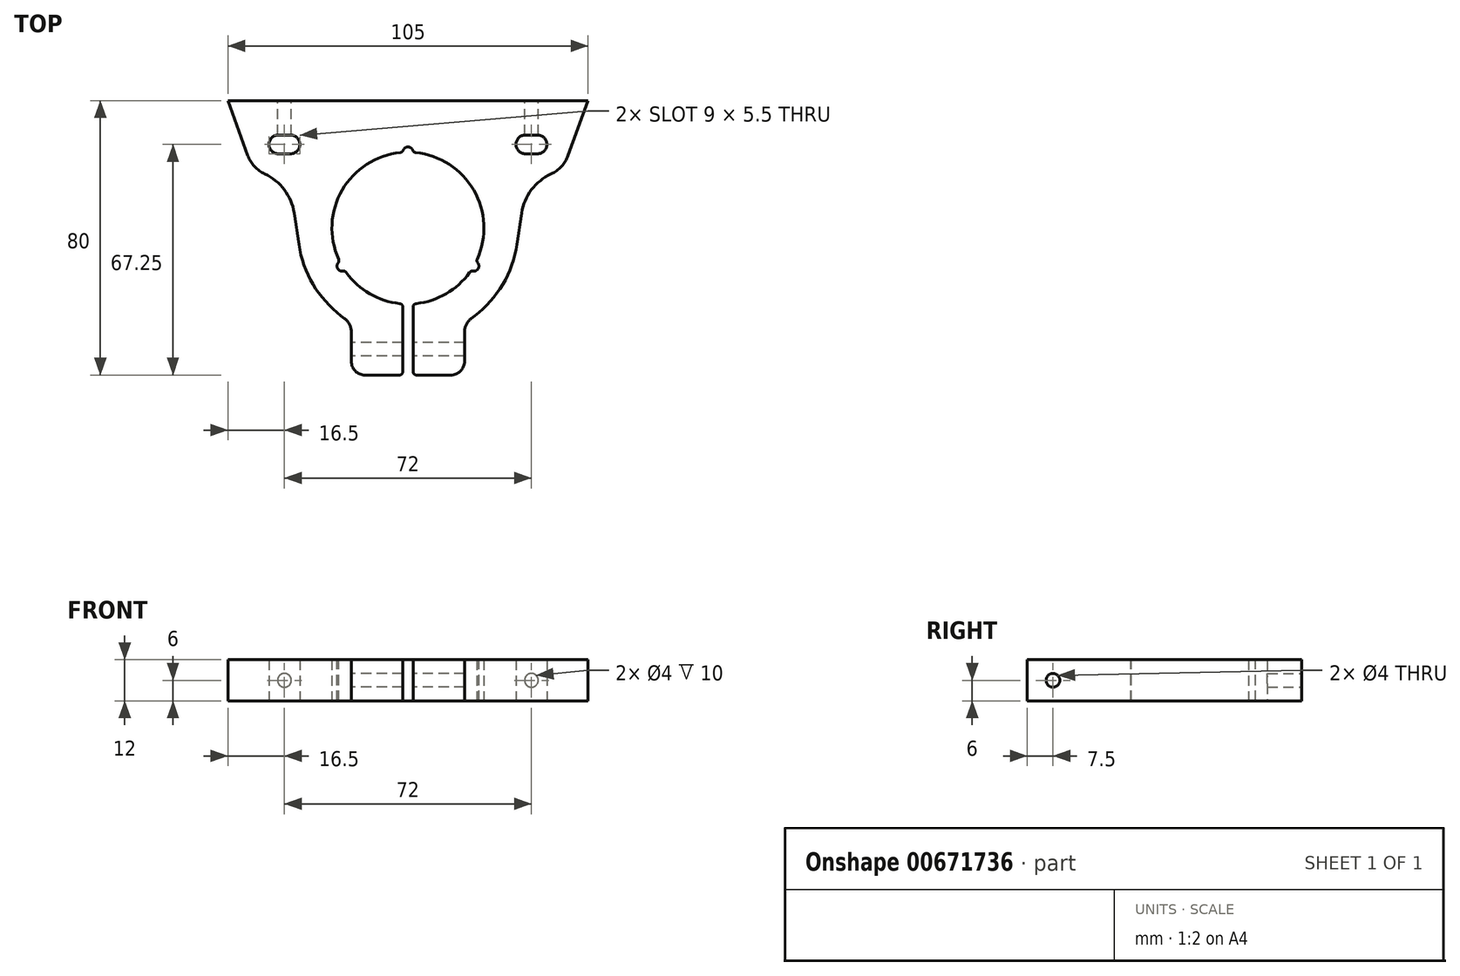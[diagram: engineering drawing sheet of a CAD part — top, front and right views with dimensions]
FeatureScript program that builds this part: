
annotation { "Feature Type Name" : "Feature", "Feature Type Description" : "" }
export const myFeature = defineFeature(function(context is Context, id is Id, definition is map)
    precondition{}
    {
        {
            var Q0;
            Q0=qCreatedBy(makeId("Top.planeOp"),FACE);
            var sketch = newSketch(context, id + "F0", { "sketchPlane" : qUnion([Q0])});
            skLineSegment(sketch, "E0", {"start": v(-52.5, 0) * mm, "end": v(52.5, 0) * mm});
            skLineSegment(sketch, "E1", {"start": v(-19.5, -62.71) * mm, "end": v(-16.5, -65) * mm});
            skLineSegment(sketch, "E2", {"start": v(-16.5, -65) * mm, "end": v(-16.5, -80) * mm});
            skLineSegment(sketch, "E3", {"start": v(-16.5, -80) * mm, "end": v(-1.5, -80) * mm});
            skLineSegment(sketch, "E4", {"start": v(-1.5, -80) * mm, "end": v(-1.5, -59.25) * mm});
            skArc(sketch, "E5", {"start": v(1.5, -59.25) * mm, "mid": v(0, -15) * mm, "end": v(-1.5, -59.25) * mm});
            skLineSegment(sketch, "E6.MirrorCS", {"start": v(16.5, -65) * mm, "end": v(16.5, -80) * mm});
            skLineSegment(sketch, "E7.MirrorCS", {"start": v(16.5, -80) * mm, "end": v(1.5, -80) * mm});
            skLineSegment(sketch, "E8.MirrorCS", {"start": v(1.5, -80) * mm, "end": v(1.5, -59.25) * mm});
            skCircle(sketch, "E9", {"center": v(0, -37.15) * mm, "radius": 32.15 * mm, "construction": true});
            skLineSegment(sketch, "E10", {"start": v(0, -37.15) * mm, "end": v(-19.5, -62.71) * mm, "construction": true});
            skLineSegment(sketch, "E11.bottom", {"start": v(-37.75, -15.5) * mm, "end": v(-34.25, -15.5) * mm});
            skLineSegment(sketch, "E11.top", {"start": v(-37.75, -10) * mm, "end": v(-34.25, -10) * mm});
            skArc(sketch, "E12", {"start": v(-37.75, -10) * mm, "mid": v(-40.5, -12.75) * mm, "end": v(-37.75, -15.5) * mm});
            skArc(sketch, "E13", {"start": v(-34.25, -15.5) * mm, "mid": v(-31.5, -12.75) * mm, "end": v(-34.25, -10) * mm});
            skLineSegment(sketch, "E14", {"start": v(0, 0) * mm, "end": v(0, -15) * mm, "construction": true});
            skLineSegment(sketch, "E15.MirrorCS", {"start": v(37.75, -15.5) * mm, "end": v(34.25, -15.5) * mm});
            skArc(sketch, "E16.MirrorCS", {"start": v(34.25, -15.5) * mm, "mid": v(31.5, -12.75) * mm, "end": v(34.25, -10) * mm});
            skArc(sketch, "E17.MirrorCS", {"start": v(37.75, -10) * mm, "mid": v(40.5, -12.75) * mm, "end": v(37.75, -15.5) * mm});
            skLineSegment(sketch, "E18.MirrorCS", {"start": v(37.75, -10) * mm, "end": v(34.25, -10) * mm});
            skArc(sketch, "E19.0", {"start": v(-46.68, -16) * mm, "mid": v(-44.74, -19.18) * mm, "end": v(-41.73, -21.38) * mm});
            skLineSegment(sketch, "E20", {"start": v(-52.5, 0) * mm, "end": v(-46.68, -16) * mm});
            skLineSegment(sketch, "E21", {"start": v(-33.17, -32.77) * mm, "end": v(-31.8, -41.94) * mm});
            skArc(sketch, "E22.MirrorCS", {"start": v(46.68, -16) * mm, "mid": v(44.74, -19.18) * mm, "end": v(41.73, -21.38) * mm});
            skLineSegment(sketch, "E23.MirrorCS", {"start": v(52.5, 0) * mm, "end": v(46.68, -16) * mm});
            skArc(sketch, "E24", {"start": v(-19.5, -62.71) * mm, "mid": v(-27.67, -53.52) * mm, "end": v(-31.8, -41.94) * mm});
            skLineSegment(sketch, "E25.MirrorCS", {"start": v(33.17, -32.77) * mm, "end": v(31.8, -41.94) * mm});
            skArc(sketch, "E26.MirrorCS", {"start": v(19.5, -62.71) * mm, "mid": v(27.67, -53.52) * mm, "end": v(31.8, -41.94) * mm});
            skLineSegment(sketch, "E27.MirrorCS", {"start": v(19.5, -62.71) * mm, "end": v(16.5, -65) * mm});
            skArc(sketch, "E28.filletArc", {"start": v(-33.17, -32.77) * mm, "mid": v(-36.01, -26) * mm, "end": v(-41.73, -21.38) * mm});
            skArc(sketch, "E29.filletArc", {"start": v(41.73, -21.38) * mm, "mid": v(36.01, -26) * mm, "end": v(33.17, -32.77) * mm});
            skSolve(sketch);
        }
        {
            var Q0;
            Q0=qSketchRegion(id+"F0",true);
            extrude(context, id + "F1", {"entities" : qUnion([Q0]), "depth" : 12 * mm, "offsetDistance" : 25 * mm});
        }
        {
            var Q0;
            Q0=makeQuery(id+"F1.opExtrude","SWEPT_EDGE",EDGE,{"disambiguationData":[OSD([sQuery(id+"F0.wireOp",EDGE,"E1"),sQuery(id+"F0.wireOp",EDGE,"E2")])]});
            var Q1;
            Q1=makeQuery(id+"F1.opExtrude","SWEPT_EDGE",EDGE,{"disambiguationData":[OSD([sQuery(id+"F0.wireOp",EDGE,"E6.MirrorCS"),sQuery(id+"F0.wireOp",EDGE,"E27.MirrorCS")])]});
            fillet(context, id + "F2", {"entities" : qUnion([Q0, Q1]), "radius" : 5 * mm, "tangentPropagation" : true, "allowEdgeOverflow" : false});
        }
        {
            var Q0;
            Q0=makeQuery(id+"F1.opExtrude","SWEPT_FACE",FACE,{"disambiguationData":[OSD([sQuery(id+"F0.wireOp",EDGE,"E2")])]});
            var sketch = newSketch(context, id + "F3", { "sketchPlane" : qUnion([Q0])});
            skCircle(sketch, "E30", {"center": v(72.5, 6) * mm, "radius": 2 * mm});
            skPoint(sketch, "E30.centerSnap0", {"position": v(80, 6) * mm});
            skSolve(sketch);
        }
        {
            var Q0;
            Q0=qSketchRegion(id+"F3",true);
            extrude(context, id + "F4", {"entities" : qUnion([Q0]), "operationType" : NewBodyOperationType.REMOVE, "endBound" : BoundingType.THROUGH_ALL, "oppositeDirection" : true, "depth" : 25 * mm, "offsetDistance" : 25 * mm});
        }
        {
            var Q0;
            Q0=makeQuery(id+"F1.opExtrude","SWEPT_EDGE",EDGE,{"disambiguationData":[OSD([sQuery(id+"F0.wireOp",EDGE,"E1"),sQuery(id+"F0.wireOp",EDGE,"E2")])]});
            var Q1;
            Q1=makeQuery(id+"F1.opExtrude","SWEPT_EDGE",EDGE,{"disambiguationData":[OSD([sQuery(id+"F0.wireOp",EDGE,"E2"),sQuery(id+"F0.wireOp",EDGE,"E3")])]});
            var Q2;
            Q2=makeQuery(id+"F1.opExtrude","SWEPT_EDGE",EDGE,{"disambiguationData":[OSD([sQuery(id+"F0.wireOp",EDGE,"E6.MirrorCS"),sQuery(id+"F0.wireOp",EDGE,"E7.MirrorCS")])]});
            var Q3;
            Q3=makeQuery(id+"F1.opExtrude","SWEPT_EDGE",EDGE,{"disambiguationData":[OSD([sQuery(id+"F0.wireOp",EDGE,"6f19a3d9-82da-4a62-acf6-6007c0667a970.MirrorCS"),sQuery(id+"F0.wireOp",EDGE,"E6.MirrorCS")])]});
            fillet(context, id + "F5", {"entities" : qUnion([Q0, Q1, Q2, Q3]), "radius" : 4 * mm, "tangentPropagation" : true, "allowEdgeOverflow" : false});
        }
        {
            var Q0;
            Q0=makeQuery(id+"F1.opExtrude","SWEPT_FACE",FACE,{"disambiguationData":[OSD([sQuery(id+"F0.wireOp",EDGE,"E0")])]});
            var sketch = newSketch(context, id + "F6", { "sketchPlane" : qUnion([Q0])});
            skCircle(sketch, "E31", {"center": v(-36, 6) * mm, "radius": 2 * mm});
            skPoint(sketch, "E31.centerSnap0", {"position": v(-52.5, 6) * mm});
            skCircle(sketch, "E32", {"center": v(36, 6) * mm, "radius": 2 * mm});
            skSolve(sketch);
        }
        {
            var Q0;
            Q0=qSketchRegion(id+"F6",true);
            extrude(context, id + "F7", {"entities" : qUnion([Q0]), "operationType" : NewBodyOperationType.REMOVE, "oppositeDirection" : true, "depth" : 12 * mm, "offsetDistance" : 25 * mm});
        }
        {
            var Q0;
            Q0=makeQuery(id+"F1.opExtrude","CAP_FACE",FACE,{"disambiguationData":[OSD([sQuery(id+"F0.wireOp",EDGE,"E0"),sQuery(id+"F0.wireOp",EDGE,"E1"),sQuery(id+"F0.wireOp",EDGE,"E2"),sQuery(id+"F0.wireOp",EDGE,"E3"),sQuery(id+"F0.wireOp",EDGE,"E4"),sQuery(id+"F0.wireOp",EDGE,"E5"),sQuery(id+"F0.wireOp",EDGE,"E6.MirrorCS"),sQuery(id+"F0.wireOp",EDGE,"E7.MirrorCS"),sQuery(id+"F0.wireOp",EDGE,"E8.MirrorCS"),sQuery(id+"F0.wireOp",EDGE,"E11.bottom"),sQuery(id+"F0.wireOp",EDGE,"E11.top"),sQuery(id+"F0.wireOp",EDGE,"E12"),sQuery(id+"F0.wireOp",EDGE,"E13"),sQuery(id+"F0.wireOp",EDGE,"E15.MirrorCS"),sQuery(id+"F0.wireOp",EDGE,"E16.MirrorCS"),sQuery(id+"F0.wireOp",EDGE,"E17.MirrorCS"),sQuery(id+"F0.wireOp",EDGE,"E18.MirrorCS"),sQuery(id+"F0.wireOp",EDGE,"E19.0"),sQuery(id+"F0.wireOp",EDGE,"E20"),sQuery(id+"F0.wireOp",EDGE,"E21"),sQuery(id+"F0.wireOp",EDGE,"E22.MirrorCS"),sQuery(id+"F0.wireOp",EDGE,"E23.MirrorCS"),sQuery(id+"F0.wireOp",EDGE,"E24"),sQuery(id+"F0.wireOp",EDGE,"E25.MirrorCS"),sQuery(id+"F0.wireOp",EDGE,"E26.MirrorCS"),sQuery(id+"F0.wireOp",EDGE,"E27.MirrorCS"),sQuery(id+"F0.wireOp",EDGE,"E28.filletArc"),sQuery(id+"F0.wireOp",EDGE,"E29.filletArc")])],"isStart":false});
            var sketch = newSketch(context, id + "F8", { "sketchPlane" : qUnion([Q0])});
            skCircle(sketch, "E33", {"center": v(0, -15) * mm, "radius": 1.5 * mm});
            skCircle(sketch, "E34.1.0", {"center": v(-19.18, -48.22) * mm, "radius": 1.5 * mm});
            skCircle(sketch, "E34.2.0", {"center": v(19.18, -48.23) * mm, "radius": 1.5 * mm});
            skPoint(sketch, "E34.center", {"position": v(0, -37.15) * mm});
            skSolve(sketch);
        }
        {
            var Q0;
            Q0=qSketchRegion(id+"F8",true);
            extrude(context, id + "F9", {"entities" : qUnion([Q0]), "operationType" : NewBodyOperationType.REMOVE, "oppositeDirection" : true, "depth" : 25 * mm, "offsetDistance" : 25 * mm});
        }
        {
            var Q0;
            Q0=makeQuery(id+"F9.boolean.opBoolean","INTERSECT",EDGE,{"disambiguationData":[OD(1.0)],"derivedFrom":[makeQuery(id+"F1.opExtrude","SWEPT_FACE",FACE,{"disambiguationData":[OSD([sQuery(id+"F0.wireOp",EDGE,"E5")])]}),makeQuery(id+"F9.opExtrude","SWEPT_FACE",FACE,{"disambiguationData":[OSD([sQuery(id+"F8.wireOp",EDGE,"E33")])]})]});
            var Q1;
            Q1=makeQuery(id+"F9.boolean.opBoolean","INTERSECT",EDGE,{"disambiguationData":[OD(0.0)],"derivedFrom":[makeQuery(id+"F1.opExtrude","SWEPT_FACE",FACE,{"disambiguationData":[OSD([sQuery(id+"F0.wireOp",EDGE,"E5")])]}),makeQuery(id+"F9.opExtrude","SWEPT_FACE",FACE,{"disambiguationData":[OSD([sQuery(id+"F8.wireOp",EDGE,"E33")])]})]});
            var Q2;
            Q2=makeQuery(id+"F9.boolean.opBoolean","INTERSECT",EDGE,{"disambiguationData":[OD(1.0)],"derivedFrom":[makeQuery(id+"F1.opExtrude","SWEPT_FACE",FACE,{"disambiguationData":[OSD([sQuery(id+"F0.wireOp",EDGE,"E5")])]}),makeQuery(id+"F9.opExtrude","SWEPT_FACE",FACE,{"disambiguationData":[OSD([sQuery(id+"F8.wireOp",EDGE,"E34.1.0")])]})]});
            var Q3;
            Q3=makeQuery(id+"F9.boolean.opBoolean","INTERSECT",EDGE,{"disambiguationData":[OD(0.0)],"derivedFrom":[makeQuery(id+"F1.opExtrude","SWEPT_FACE",FACE,{"disambiguationData":[OSD([sQuery(id+"F0.wireOp",EDGE,"E5")])]}),makeQuery(id+"F9.opExtrude","SWEPT_FACE",FACE,{"disambiguationData":[OSD([sQuery(id+"F8.wireOp",EDGE,"E34.1.0")])]})]});
            var Q4;
            Q4=makeQuery(id+"F9.boolean.opBoolean","INTERSECT",EDGE,{"disambiguationData":[OD(0.0)],"derivedFrom":[makeQuery(id+"F1.opExtrude","SWEPT_FACE",FACE,{"disambiguationData":[OSD([sQuery(id+"F0.wireOp",EDGE,"E5")])]}),makeQuery(id+"F9.opExtrude","SWEPT_FACE",FACE,{"disambiguationData":[OSD([sQuery(id+"F8.wireOp",EDGE,"E34.2.0")])]})]});
            var Q5;
            Q5=makeQuery(id+"F9.boolean.opBoolean","INTERSECT",EDGE,{"disambiguationData":[OD(1.0)],"derivedFrom":[makeQuery(id+"F1.opExtrude","SWEPT_FACE",FACE,{"disambiguationData":[OSD([sQuery(id+"F0.wireOp",EDGE,"E5")])]}),makeQuery(id+"F9.opExtrude","SWEPT_FACE",FACE,{"disambiguationData":[OSD([sQuery(id+"F8.wireOp",EDGE,"E34.2.0")])]})]});
            var Q6;
            Q6=makeQuery(id+"F1.opExtrude","SWEPT_EDGE",EDGE,{"disambiguationData":[OSD([sQuery(id+"F0.wireOp",EDGE,"E5"),sQuery(id+"F0.wireOp",EDGE,"E8.MirrorCS")])]});
            var Q7;
            Q7=makeQuery(id+"F1.opExtrude","SWEPT_EDGE",EDGE,{"disambiguationData":[OSD([sQuery(id+"F0.wireOp",EDGE,"E4"),sQuery(id+"F0.wireOp",EDGE,"E5")])]});
            var Q8;
            Q8=makeQuery(id+"F1.opExtrude","SWEPT_EDGE",EDGE,{"disambiguationData":[OSD([sQuery(id+"F0.wireOp",EDGE,"E7.MirrorCS"),sQuery(id+"F0.wireOp",EDGE,"E8.MirrorCS")])]});
            var Q9;
            Q9=makeQuery(id+"F1.opExtrude","SWEPT_EDGE",EDGE,{"disambiguationData":[OSD([sQuery(id+"F0.wireOp",EDGE,"E3"),sQuery(id+"F0.wireOp",EDGE,"E4")])]});
            fillet(context, id + "F10", {"entities" : qUnion([Q0, Q1, Q2, Q3, Q4, Q5, Q6, Q7, Q8, Q9]), "radius" : 1 * mm, "tangentPropagation" : true, "allowEdgeOverflow" : false});
        }
    });
